# Revit family: ledflood-e3_re345-200w-840-bl-as_709000116700
name_source: partatom
category: Lighting Fixtures
units: mm (PartAtom-declared; Revit-internal decimal feet)

## family parameters
Cut with Voids When Loaded = No
Host = Face
Light Source = No
Part Type = Normal
Room Calculation Point = No
Round Connector Dimension = Use Diameter
Shared = No

## types (1)
- LEDFlood-E3 Re345-200W-840-BL-AS (1 x LED, 30000 lm, 4000)
    Apparent Load = 200 VA
    CIE Flux Codes = 54 91 99 100 100
    Color Rendering = 80
    Color Temperature = 4000
    Control Gear = Electronic ballast
    Default Elevation = 1800 mm
    Description = Floodlight EcoMax G3 200W-30000lm-4000K
    Height = 50 mm
    Lamp = 1 x LED
    Lamp Light Flux = 30000 lm
    Lamp count = 1
    Length = 400 mm
    Luminous efficacy = 150 lm/W
    Manufacturer = OPPLE
    ModVariant = No
    Model = 709000116700
    Mounting Place = Ceiling
    Mounting Type = Surface mounted
    Number of Poles = 1
    OnlyDefault = Yes
    Power Factor = 1
    Product Name = LEDFlood-E3 Re345-200W-840-BL-AS
    Product group = Filament A60
    ProductGroupID = 310
    Protection Class = Protection class I
    Protection Degree = IP 66
    RLX_Detail_Level = 1
    RLX_Emergency_Light_Flux = 0 lm
    RLX_Emergency_Type = 0
    RLX_Emergency_Type_DB = No
    RlxData = <blob elided: 259765 chars, md5=d24ba73c>
    Socket = socket
    Standby Power = 0 W
    System Light Flux = 30000 lm
    System Power = 200 W
    Type Comments = Product without accessories
    Type Image = web_fl_eco_g3_as.jpg
    URL = http://relux.com
    VarID = ---
    Voltage = 0 V
    Weight = 0.00 kg
    Width = 333 mm

## geometry (parser evidence)
native form markers: Blend x4, Sweep x13
no freeform markers — native parametric forms only
